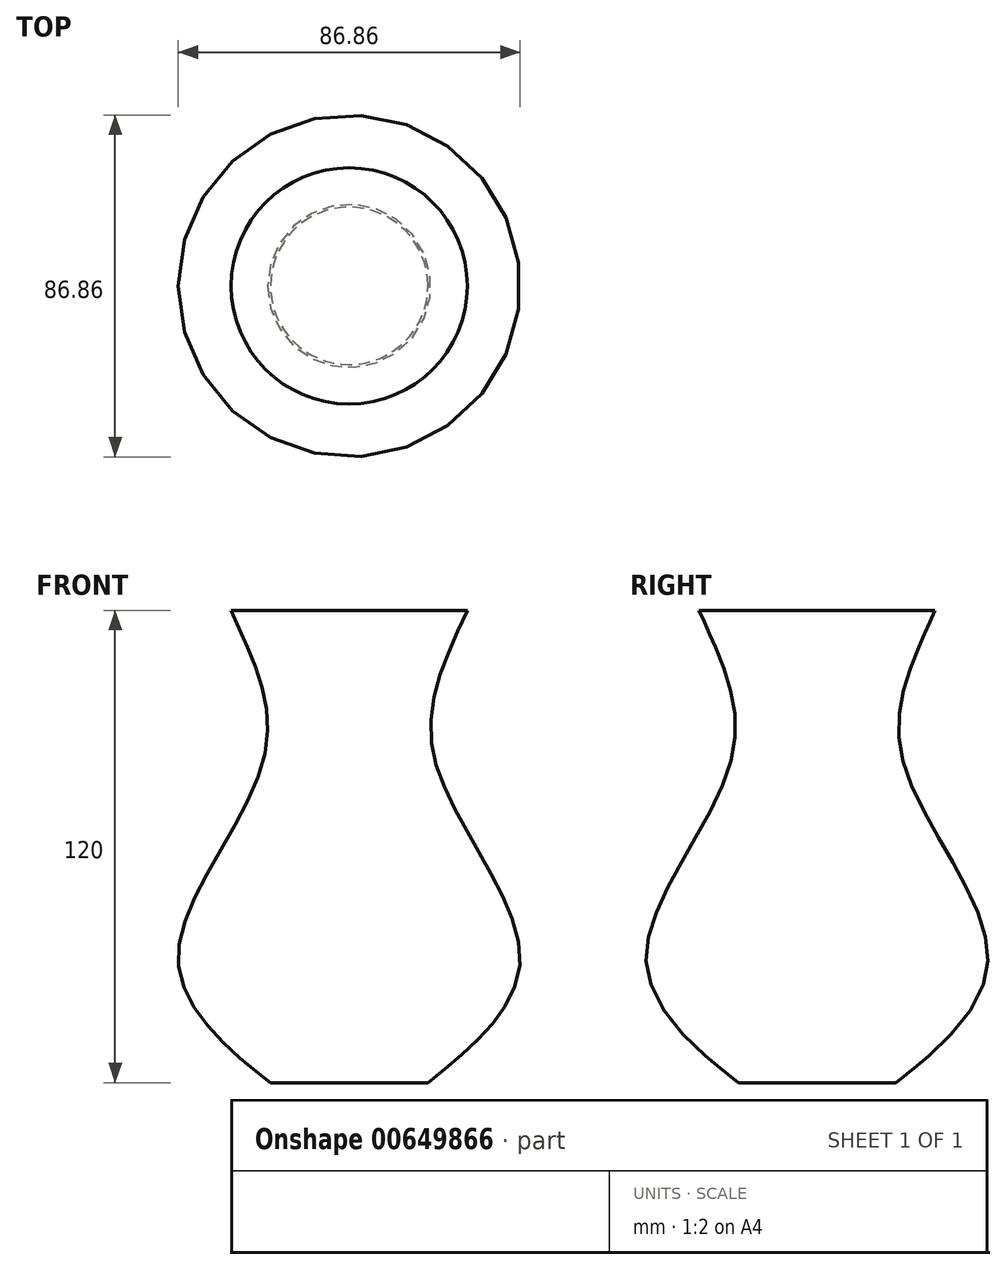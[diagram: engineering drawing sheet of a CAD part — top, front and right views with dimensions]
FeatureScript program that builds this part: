
annotation { "Feature Type Name" : "Feature", "Feature Type Description" : "" }
export const myFeature = defineFeature(function(context is Context, id is Id, definition is map)
    precondition{}
    {
        {
            var Q0;
            Q0=qCreatedBy(makeId("Front.planeOp"),FACE);
            var sketch = newSketch(context, id + "F0", { "sketchPlane" : qUnion([Q0])});
            skLineSegment(sketch, "E0", {"start": v(0, 0) * mm, "end": v(0, 120) * mm});
            skLineSegment(sketch, "E1", {"start": v(0, 0) * mm, "end": v(20, 0) * mm});
            skLineSegment(sketch, "E2", {"start": v(0, 120) * mm, "end": v(0, 107.44) * mm});
            skFitSpline(sketch, "E3", {"points": [v(20, 0) * mm, v(43.38, 30.36) * mm, v(21.52, 82.92) * mm, v(30, 120) * mm], "startDerivative": vector(77.81, 61.46) * mm, "endDerivative": vector(45.48, 103.7) * mm});
            skLineSegment(sketch, "E4", {"start": v(0, 120) * mm, "end": v(30, 120) * mm});
            skSolve(sketch);
        }
        {
            var Q0;
            Q0=makeQuery(id+"F0.imprint","IMPRINT",FACE,{"disambiguationData":[TD([[makeQuery(id+"F0.imprint","IMPRINT",EDGE,{"derivedFrom":sQuery(id+"F0.wireOp",EDGE,"E0")}),-1.0]])]});
            var Q1;
            Q1=sQuery(id+"F0.wireOp",EDGE,"E0");
            revolve(context, id + "F1", {"entities" : qUnion([Q0]), "axis" : qUnion([Q1]), "revolveType" : RevolveType.FULL});
        }
    });
